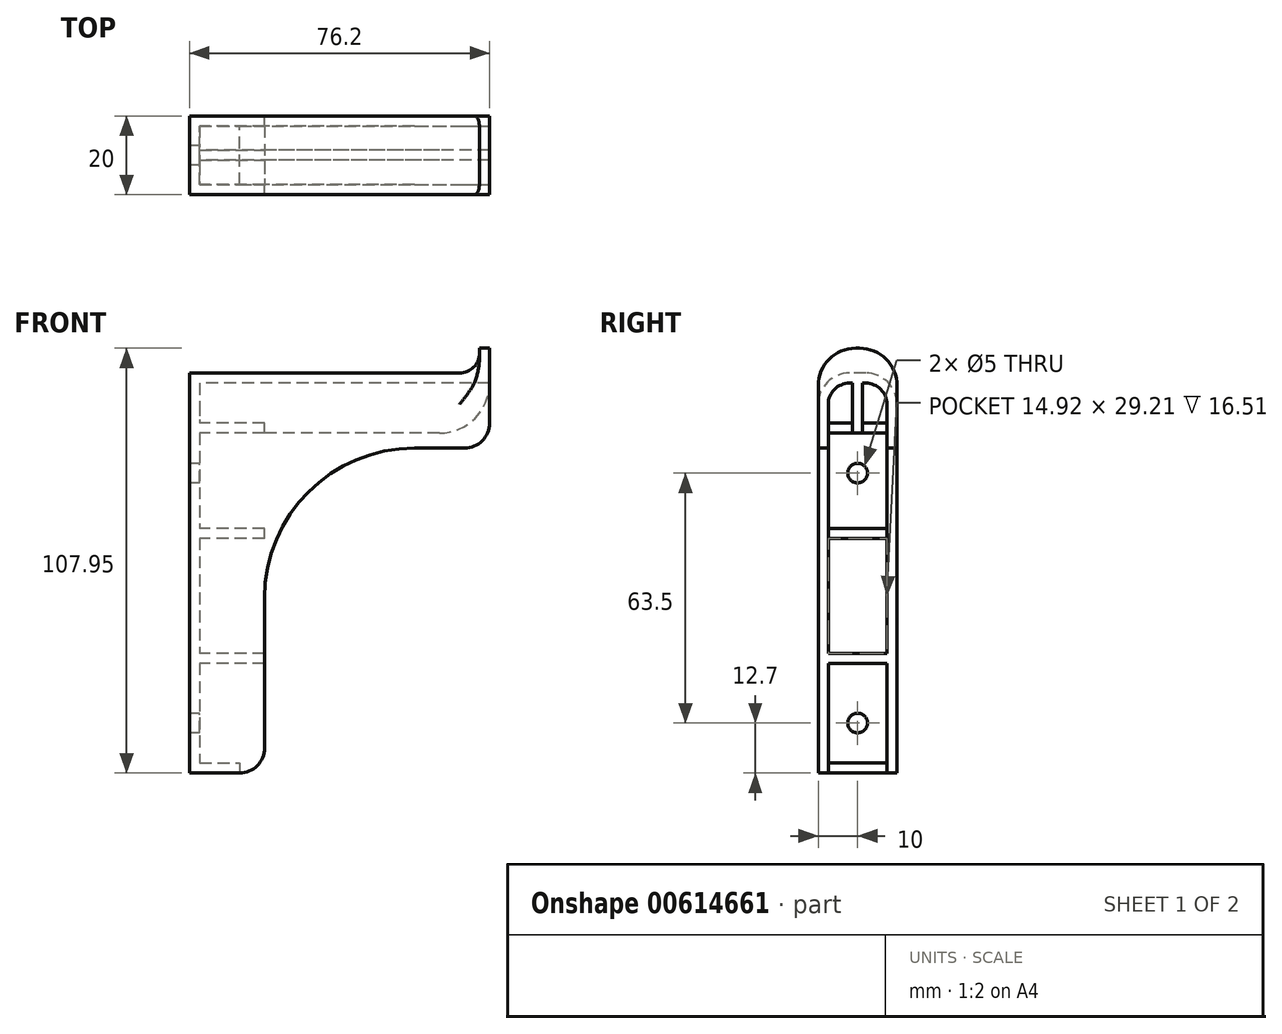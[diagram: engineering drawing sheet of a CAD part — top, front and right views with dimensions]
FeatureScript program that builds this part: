
annotation { "Feature Type Name" : "Feature", "Feature Type Description" : "" }
export const myFeature = defineFeature(function(context is Context, id is Id, definition is map)
    precondition{}
    {
        {
            var Q0;
            Q0=qCreatedBy(makeId("Front.planeOp"),FACE);
            var sketch = newSketch(context, id + "F0", { "sketchPlane" : qUnion([Q0])});
            skLineSegment(sketch, "E0", {"start": v(0, 0) * mm, "end": v(0, -101.6) * mm});
            skLineSegment(sketch, "E1", {"start": v(0, -101.6) * mm, "end": v(12.7, -101.6) * mm});
            skLineSegment(sketch, "E2", {"start": v(19.05, -95.25) * mm, "end": v(19.05, -57.15) * mm});
            skLineSegment(sketch, "E3", {"start": v(57.15, -19.05) * mm, "end": v(69.85, -19.05) * mm});
            skLineSegment(sketch, "E4", {"start": v(76.2, -12.7) * mm, "end": v(76.2, 0) * mm});
            skLineSegment(sketch, "E5", {"start": v(76.2, 0) * mm, "end": v(0, 0) * mm});
            skPoint(sketch, "E6.visualSharp", {"position": v(19.05, -19.05) * mm});
            skArc(sketch, "E6.filletArc", {"start": v(57.15, -19.05) * mm, "mid": v(30.2, -30.2) * mm, "end": v(19.05, -57.15) * mm});
            skPoint(sketch, "E7.visualSharp", {"position": v(19.05, -101.6) * mm});
            skArc(sketch, "E7.filletArc", {"start": v(12.7, -101.6) * mm, "mid": v(17.2, -99.74) * mm, "end": v(19.05, -95.25) * mm});
            skPoint(sketch, "E8.visualSharp", {"position": v(76.2, -19.05) * mm});
            skArc(sketch, "E8.filletArc", {"start": v(69.85, -19.05) * mm, "mid": v(74.34, -17.2) * mm, "end": v(76.2, -12.7) * mm});
            skSolve(sketch);
        }
        {
            var Q0;
            Q0 = qSketchRegion(id + "F0", true);
            extrude(context, id + "F1", {"entities" : qUnion([Q0]), "endBound" : BoundingType.SYMMETRIC, "depth" : 20 * mm, "offsetDistance" : 25.4 * mm});
        }
        {
            var Q0;
            Q0=makeQuery(id+"F1.opExtrude","CAP_EDGE",EDGE,{"disambiguationData":[OSD([sQuery(id+"F0.wireOp",EDGE,"E5")])],"isStart":false});
            var Q1;
            Q1=makeQuery(id+"F1.opExtrude","CAP_EDGE",EDGE,{"disambiguationData":[OSD([sQuery(id+"F0.wireOp",EDGE,"E5")])],"isStart":true});
            fillet(context, id + "F2", {"entities" : qUnion([Q0, Q1]), "radius" : 7.94 * mm, "tangentPropagation" : true, "allowEdgeOverflow" : false});
        }
        {
            var Q0;
            Q0=makeQuery(id+"F1.opExtrude","SWEPT_FACE",FACE,{"disambiguationData":[OSD([sQuery(id+"F0.wireOp",EDGE,"E0")])]});
            var sketch = newSketch(context, id + "F3", { "sketchPlane" : qUnion([Q0])});
            skCircle(sketch, "E9", {"center": v(0, -25.4) * mm, "radius": 2.5 * mm});
            skCircle(sketch, "E10", {"center": v(0, -88.9) * mm, "radius": 2.5 * mm});
            skSolve(sketch);
        }
        {
            var Q0;
            Q0 = qSketchRegion(id + "F3", true);
            extrude(context, id + "F4", {"entities" : qUnion([Q0]), "operationType" : NewBodyOperationType.REMOVE, "endBound" : BoundingType.THROUGH_ALL, "oppositeDirection" : true, "depth" : 25.4 * mm, "offsetDistance" : 25.4 * mm});
        }
        {
            var Q0;
            Q0=makeQuery(id+"F4.boolean.opBoolean","COPY",FACE,{"derivedFrom":makeQuery(id+"F4.opExtrude","SWEPT_FACE",FACE,{"disambiguationData":[OSD([sQuery(id+"F3.wireOp",EDGE,"E9")])]})});
            var Q1;
            Q1=makeQuery(id+"F1.opExtrude","SWEPT_FACE",FACE,{"disambiguationData":[OSD([sQuery(id+"F0.wireOp",EDGE,"E3")])]});
            var Q2;
            Q2=makeQuery(id+"F1.opExtrude","SWEPT_FACE",FACE,{"disambiguationData":[OSD([sQuery(id+"F0.wireOp",EDGE,"E6.filletArc")])]});
            var Q3;
            Q3=makeQuery(id+"F1.opExtrude","SWEPT_FACE",FACE,{"disambiguationData":[OSD([sQuery(id+"F0.wireOp",EDGE,"E2")])]});
            var Q4;
            Q4=makeQuery(id+"F1.opExtrude","SWEPT_FACE",FACE,{"disambiguationData":[OSD([sQuery(id+"F0.wireOp",EDGE,"E7.filletArc")])]});
            var Q5;
            Q5=makeQuery(id+"F4.boolean.opBoolean","COPY",FACE,{"derivedFrom":makeQuery(id+"F4.opExtrude","SWEPT_FACE",FACE,{"disambiguationData":[OSD([sQuery(id+"F3.wireOp",EDGE,"E10")])]})});
            var Q6;
            Q6=makeQuery(id+"F1.opExtrude","SWEPT_FACE",FACE,{"disambiguationData":[OSD([sQuery(id+"F0.wireOp",EDGE,"E8.filletArc")])]});
            var Q7;
            Q7=makeQuery(id+"F1.opExtrude","SWEPT_FACE",FACE,{"disambiguationData":[OSD([sQuery(id+"F0.wireOp",EDGE,"E4")])]});
            shell(context, id + "F5", {"entities" : qUnion([Q0, Q1, Q2, Q3, Q4, Q5, Q6, Q7]), "thickness" : 2.54 * mm});
        }
        {
            var Q0;
            Q0=makeQuery(id+"F5.opShell","OFFSET_FACE",FACE,{"disambiguationData":[OSD([sQuery(id+"F0.wireOp",EDGE,"E0")])]});
            var sketch = newSketch(context, id + "F6", { "sketchPlane" : qUnion([Q0])});
            skLineSegment(sketch, "E11.bottom", {"start": v(-1.27, -2.54) * mm, "end": v(1.27, -2.54) * mm});
            skLineSegment(sketch, "E11.top", {"start": v(-1.27, -15.24) * mm, "end": v(1.27, -15.24) * mm});
            skLineSegment(sketch, "E11.left", {"start": v(-1.27, -2.54) * mm, "end": v(-1.27, -15.24) * mm});
            skLineSegment(sketch, "E11.right", {"start": v(1.27, -2.54) * mm, "end": v(1.27, -15.24) * mm});
            skLineSegment(sketch, "E12", {"start": v(0, -2.54) * mm, "end": v(0, -15.24) * mm, "construction": true});
            skSolve(sketch);
        }
        {
            var Q0;
            Q0 = qSketchRegion(id + "F6", true);
            var Q1;
            Q1=makeQuery(id+"F1.opExtrude","SWEPT_FACE",FACE,{"disambiguationData":[OSD([sQuery(id+"F0.wireOp",EDGE,"E4")])]});
            extrude(context, id + "F7", {"entities" : qUnion([Q0]), "operationType" : NewBodyOperationType.ADD, "endBound" : BoundingType.UP_TO_SURFACE, "depth" : 25.4 * mm, "endBoundEntityFace" : qUnion([Q1]), "offsetDistance" : 25.4 * mm});
        }
        {
            var Q0;
            Q0=makeQuery(id+"F7.opExtrude","CAP_EDGE",EDGE,{"disambiguationData":[OSD([sQuery(id+"F6.wireOp",EDGE,"E11.top")])],"isStart":false});
            fillet(context, id + "F8", {"entities" : qUnion([Q0]), "radius" : 12.7 * mm, "tangentPropagation" : true, "allowEdgeOverflow" : false});
        }
        {
            var Q0;
            Q0=makeQuery(id+"F7.boolean.opBoolean","MERGE",FACE,{"derivedFrom":[makeQuery(id+"F1.opExtrude","SWEPT_FACE",FACE,{"disambiguationData":[OSD([sQuery(id+"F0.wireOp",EDGE,"E4")])]}),makeQuery(id+"F7.opExtrude","CAP_FACE",FACE,{"disambiguationData":[OSD([sQuery(id+"F6.wireOp",EDGE,"E11.bottom"),sQuery(id+"F6.wireOp",EDGE,"E11.top"),sQuery(id+"F6.wireOp",EDGE,"E11.left"),sQuery(id+"F6.wireOp",EDGE,"E11.right")])],"isStart":false})]});
            var sketch = newSketch(context, id + "F9", { "sketchPlane" : qUnion([Q0])});
            skLineSegment(sketch, "E13", {"start": v(10, -7.94) * mm, "end": v(10, -3.17) * mm});
            skLineSegment(sketch, "E14", {"start": v(0.47, 6.35) * mm, "end": v(-0.47, 6.35) * mm});
            skLineSegment(sketch, "E15", {"start": v(-10, -3.18) * mm, "end": v(-10, -7.94) * mm});
            skPoint(sketch, "E16.visualSharp", {"position": v(10, 6.35) * mm});
            skArc(sketch, "E16.filletArc", {"start": v(10, -3.17) * mm, "mid": v(7.21, 3.56) * mm, "end": v(0.47, 6.35) * mm});
            skPoint(sketch, "E17.visualSharp", {"position": v(-10, 6.35) * mm});
            skArc(sketch, "E17.filletArc", {"start": v(-0.47, 6.35) * mm, "mid": v(-7.21, 3.56) * mm, "end": v(-10, -3.17) * mm});
            skLineSegment(sketch, "E18.0", {"start": v(10, -12.7) * mm, "end": v(10, -7.94) * mm});
            skLineSegment(sketch, "E18.1", {"start": v(7.46, -12.7) * mm, "end": v(10, -12.7) * mm});
            skLineSegment(sketch, "E18.2", {"start": v(7.46, -12.7) * mm, "end": v(7.46, -7.94) * mm});
            skArc(sketch, "E18.3", {"start": v(7.46, -7.94) * mm, "mid": v(5.88, -4.12) * mm, "end": v(2.06, -2.54) * mm});
            skLineSegment(sketch, "E18.4", {"start": v(1.27, -2.54) * mm, "end": v(2.06, -2.54) * mm});
            skLineSegment(sketch, "E18.5", {"start": v(-1.27, -2.54) * mm, "end": v(1.27, -2.54) * mm});
            skLineSegment(sketch, "E18.6", {"start": v(-2.06, -2.54) * mm, "end": v(-1.27, -2.54) * mm});
            skArc(sketch, "E18.7", {"start": v(-2.06, -2.54) * mm, "mid": v(-5.88, -4.12) * mm, "end": v(-7.46, -7.94) * mm});
            skLineSegment(sketch, "E18.8", {"start": v(-7.46, -12.7) * mm, "end": v(-7.46, -7.94) * mm});
            skLineSegment(sketch, "E18.9", {"start": v(-10, -12.7) * mm, "end": v(-7.46, -12.7) * mm});
            skLineSegment(sketch, "E18.10", {"start": v(-10, -12.7) * mm, "end": v(-10, -7.94) * mm});
            skSolve(sketch);
        }
        {
            var Q0;
            Q0 = qSketchRegion(id + "F9", true);
            extrude(context, id + "F10", {"entities" : qUnion([Q0]), "operationType" : NewBodyOperationType.ADD, "oppositeDirection" : true, "depth" : 2.54 * mm, "offsetDistance" : 25.4 * mm});
        }
        {
            var Q0;
            {var subQ0=sQuery(id+"F0.wireOp",EDGE,"E5");Q0=makeQuery(id+"F10.boolean.opBoolean","INTERSECT",EDGE,{"derivedFrom":[makeQuery(id+"F2.opFillet","BLEND_FACE",FACE,{"disambiguationData":[OSD([subQ0]),TDD([makeQuery(id+"F1.opExtrude","CAP_EDGE",EDGE,{"disambiguationData":[OSD([subQ0])],"isStart":false})])]}),makeQuery(id+"F10.opExtrude","CAP_FACE",FACE,{"disambiguationData":[OSD([sQuery(id+"F9.wireOp",EDGE,"E13"),sQuery(id+"F9.wireOp",EDGE,"E14"),sQuery(id+"F9.wireOp",EDGE,"E15"),sQuery(id+"F9.wireOp",EDGE,"E16.filletArc"),sQuery(id+"F9.wireOp",EDGE,"E17.filletArc"),sQuery(id+"F9.wireOp",EDGE,"E18.0"),sQuery(id+"F9.wireOp",EDGE,"E18.1"),sQuery(id+"F9.wireOp",EDGE,"E18.2"),sQuery(id+"F9.wireOp",EDGE,"E18.3"),sQuery(id+"F9.wireOp",EDGE,"E18.4"),sQuery(id+"F9.wireOp",EDGE,"E18.5"),sQuery(id+"F9.wireOp",EDGE,"E18.6"),sQuery(id+"F9.wireOp",EDGE,"E18.7"),sQuery(id+"F9.wireOp",EDGE,"E18.8"),sQuery(id+"F9.wireOp",EDGE,"E18.9"),sQuery(id+"F9.wireOp",EDGE,"E18.10")])],"isStart":false})]});}
            var Q1;
            Q1=makeQuery(id+"F10.boolean.opBoolean","INTERSECT",EDGE,{"derivedFrom":[makeQuery(id+"F1.opExtrude","SWEPT_FACE",FACE,{"disambiguationData":[OSD([sQuery(id+"F0.wireOp",EDGE,"E5")])]}),makeQuery(id+"F10.opExtrude","CAP_FACE",FACE,{"disambiguationData":[OSD([sQuery(id+"F9.wireOp",EDGE,"E13"),sQuery(id+"F9.wireOp",EDGE,"E14"),sQuery(id+"F9.wireOp",EDGE,"E15"),sQuery(id+"F9.wireOp",EDGE,"E16.filletArc"),sQuery(id+"F9.wireOp",EDGE,"E17.filletArc"),sQuery(id+"F9.wireOp",EDGE,"E18.0"),sQuery(id+"F9.wireOp",EDGE,"E18.1"),sQuery(id+"F9.wireOp",EDGE,"E18.2"),sQuery(id+"F9.wireOp",EDGE,"E18.3"),sQuery(id+"F9.wireOp",EDGE,"E18.4"),sQuery(id+"F9.wireOp",EDGE,"E18.5"),sQuery(id+"F9.wireOp",EDGE,"E18.6"),sQuery(id+"F9.wireOp",EDGE,"E18.7"),sQuery(id+"F9.wireOp",EDGE,"E18.8"),sQuery(id+"F9.wireOp",EDGE,"E18.9"),sQuery(id+"F9.wireOp",EDGE,"E18.10")])],"isStart":false})]});
            var Q2;
            {var subQ0=sQuery(id+"F0.wireOp",EDGE,"E5");Q2=makeQuery(id+"F10.boolean.opBoolean","INTERSECT",EDGE,{"derivedFrom":[makeQuery(id+"F2.opFillet","BLEND_FACE",FACE,{"disambiguationData":[OSD([subQ0]),TDD([makeQuery(id+"F1.opExtrude","CAP_EDGE",EDGE,{"disambiguationData":[OSD([subQ0])],"isStart":true})])]}),makeQuery(id+"F10.opExtrude","CAP_FACE",FACE,{"disambiguationData":[OSD([sQuery(id+"F9.wireOp",EDGE,"E13"),sQuery(id+"F9.wireOp",EDGE,"E14"),sQuery(id+"F9.wireOp",EDGE,"E15"),sQuery(id+"F9.wireOp",EDGE,"E16.filletArc"),sQuery(id+"F9.wireOp",EDGE,"E17.filletArc"),sQuery(id+"F9.wireOp",EDGE,"E18.0"),sQuery(id+"F9.wireOp",EDGE,"E18.1"),sQuery(id+"F9.wireOp",EDGE,"E18.2"),sQuery(id+"F9.wireOp",EDGE,"E18.3"),sQuery(id+"F9.wireOp",EDGE,"E18.4"),sQuery(id+"F9.wireOp",EDGE,"E18.5"),sQuery(id+"F9.wireOp",EDGE,"E18.6"),sQuery(id+"F9.wireOp",EDGE,"E18.7"),sQuery(id+"F9.wireOp",EDGE,"E18.8"),sQuery(id+"F9.wireOp",EDGE,"E18.9"),sQuery(id+"F9.wireOp",EDGE,"E18.10")])],"isStart":false})]});}
            fillet(context, id + "F11", {"entities" : qUnion([Q0, Q1, Q2]), "radius" : 5.08 * mm, "tangentPropagation" : true, "allowEdgeOverflow" : false});
        }
        {
            var Q0;
            Q0=makeQuery(id+"F5.opShell","OFFSET_FACE",FACE,{"disambiguationData":[OSD([sQuery(id+"F0.wireOp",EDGE,"E0")])]});
            var sketch = newSketch(context, id + "F12", { "sketchPlane" : qUnion([Q0])});
            skLineSegment(sketch, "E19.bottom", {"start": v(-7.46, -39.41) * mm, "end": v(7.46, -39.41) * mm});
            skLineSegment(sketch, "E19.top", {"start": v(-7.46, -41.95) * mm, "end": v(7.46, -41.95) * mm});
            skLineSegment(sketch, "E19.left", {"start": v(-7.46, -39.41) * mm, "end": v(-7.46, -41.95) * mm});
            skLineSegment(sketch, "E19.right", {"start": v(7.46, -39.41) * mm, "end": v(7.46, -41.95) * mm});
            skLineSegment(sketch, "E20.bottom", {"start": v(-7.46, -71.16) * mm, "end": v(7.46, -71.16) * mm});
            skLineSegment(sketch, "E20.top", {"start": v(-7.46, -73.7) * mm, "end": v(7.46, -73.7) * mm});
            skLineSegment(sketch, "E20.left", {"start": v(-7.46, -71.16) * mm, "end": v(-7.46, -73.7) * mm});
            skLineSegment(sketch, "E20.right", {"start": v(7.46, -71.16) * mm, "end": v(7.46, -73.7) * mm});
            skLineSegment(sketch, "E21.bottom", {"start": v(-7.46, -15.24) * mm, "end": v(7.46, -15.24) * mm});
            skLineSegment(sketch, "E21.top", {"start": v(-7.46, -12.7) * mm, "end": v(7.46, -12.7) * mm});
            skLineSegment(sketch, "E21.left", {"start": v(-7.46, -15.24) * mm, "end": v(-7.46, -12.7) * mm});
            skLineSegment(sketch, "E21.right", {"start": v(7.46, -15.24) * mm, "end": v(7.46, -12.7) * mm});
            skSolve(sketch);
        }
        {
            var Q0;
            Q0 = qSketchRegion(id + "F12", true);
            var Q1;
            Q1=makeQuery(id+"F1.opExtrude","SWEPT_FACE",FACE,{"disambiguationData":[OSD([sQuery(id+"F0.wireOp",EDGE,"E2")])]});
            extrude(context, id + "F13", {"entities" : qUnion([Q0]), "operationType" : NewBodyOperationType.ADD, "endBound" : BoundingType.UP_TO_SURFACE, "depth" : 25.4 * mm, "endBoundEntityFace" : qUnion([Q1]), "offsetDistance" : 25.4 * mm});
        }
    });
